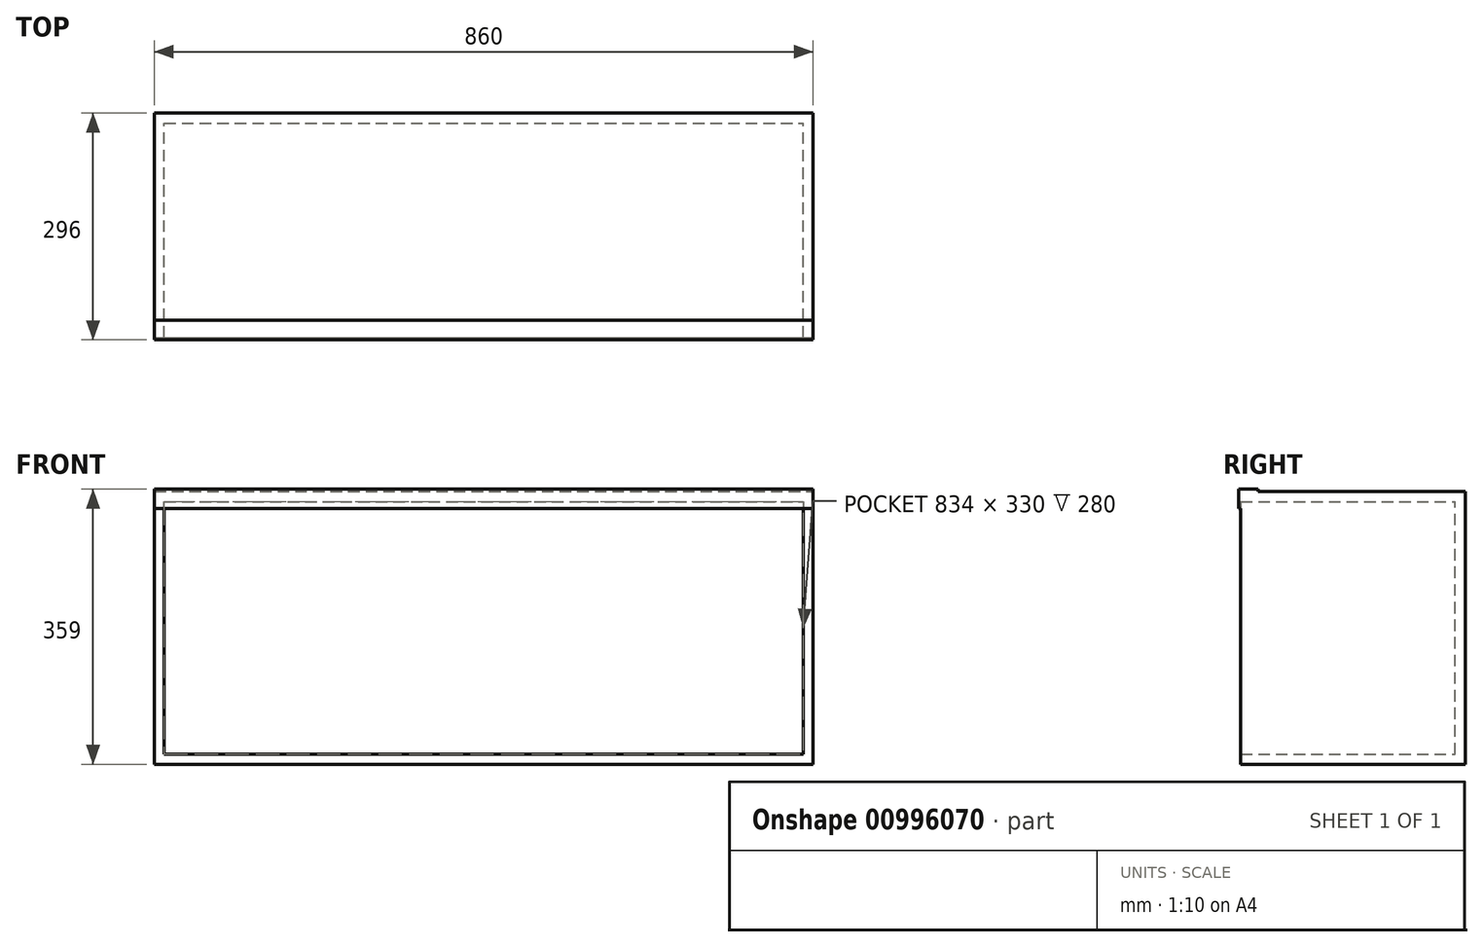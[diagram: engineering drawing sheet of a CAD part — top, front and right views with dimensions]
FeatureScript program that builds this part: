
annotation { "Feature Type Name" : "Feature", "Feature Type Description" : "" }
export const myFeature = defineFeature(function(context is Context, id is Id, definition is map)
    precondition{}
    {
        {
            var Q0;
            Q0=qCreatedBy(makeId("Front.planeOp"),FACE);
            var sketch = newSketch(context, id + "F0", { "sketchPlane" : qUnion([Q0])});
            skLineSegment(sketch, "E0.bottom", {"start": v(-430, 178) * mm, "end": v(430, 178) * mm});
            skLineSegment(sketch, "E0.top", {"start": v(-430, -178) * mm, "end": v(430, -178) * mm});
            skLineSegment(sketch, "E0.left", {"start": v(-430, 178) * mm, "end": v(-430, -178) * mm});
            skLineSegment(sketch, "E0.right", {"start": v(430, 178) * mm, "end": v(430, -178) * mm});
            skPoint(sketch, "E0.middle", {"position": v(0, 0) * mm});
            skSolve(sketch);
        }
        {
            var Q0;
            Q0 = qSketchRegion(id + "F0", true);
            extrude(context, id + "F1", {"entities" : qUnion([Q0]), "depth" : 13 * mm, "offsetDistance" : 25.4 * mm});
        }
        {
            var Q0;
            Q0=makeQuery(id+"F1.opExtrude","CAP_FACE",FACE,{"disambiguationData":[OSD([sQuery(id+"F0.wireOp",EDGE,"E0.bottom"),sQuery(id+"F0.wireOp",EDGE,"E0.top"),sQuery(id+"F0.wireOp",EDGE,"E0.left"),sQuery(id+"F0.wireOp",EDGE,"E0.right")])],"isStart":false});
            var sketch = newSketch(context, id + "F2", { "sketchPlane" : qUnion([Q0])});
            skLineSegment(sketch, "E1.bottom", {"start": v(-430, -178) * mm, "end": v(-417, -178) * mm});
            skLineSegment(sketch, "E1.top", {"start": v(-430, 178) * mm, "end": v(-417, 178) * mm});
            skLineSegment(sketch, "E1.left", {"start": v(-430, -178) * mm, "end": v(-430, 178) * mm});
            skLineSegment(sketch, "E1.right", {"start": v(-417, -178) * mm, "end": v(-417, 178) * mm});
            skLineSegment(sketch, "E2.bottom", {"start": v(430, 178) * mm, "end": v(417, 178) * mm});
            skLineSegment(sketch, "E2.top", {"start": v(430, -178) * mm, "end": v(417, -178) * mm});
            skLineSegment(sketch, "E2.left", {"start": v(430, 178) * mm, "end": v(430, -178) * mm});
            skLineSegment(sketch, "E2.right", {"start": v(417, 178) * mm, "end": v(417, -178) * mm});
            skSolve(sketch);
        }
        {
            var Q0;
            Q0 = qSketchRegion(id + "F2", true);
            extrude(context, id + "F3", {"entities" : qUnion([Q0]), "operationType" : NewBodyOperationType.ADD, "depth" : 280 * mm, "offsetDistance" : 25.4 * mm});
        }
        {
            var Q0;
            Q0=makeQuery(id+"F1.opExtrude","CAP_FACE",FACE,{"disambiguationData":[OSD([sQuery(id+"F0.wireOp",EDGE,"E0.bottom"),sQuery(id+"F0.wireOp",EDGE,"E0.top"),sQuery(id+"F0.wireOp",EDGE,"E0.left"),sQuery(id+"F0.wireOp",EDGE,"E0.right")])],"isStart":false});
            var sketch = newSketch(context, id + "F4", { "sketchPlane" : qUnion([Q0])});
            skLineSegment(sketch, "E3.bottom", {"start": v(-417, 178) * mm, "end": v(417, 178) * mm});
            skLineSegment(sketch, "E3.top", {"start": v(-417, 165) * mm, "end": v(417, 165) * mm});
            skLineSegment(sketch, "E3.left", {"start": v(-417, 178) * mm, "end": v(-417, 165) * mm});
            skLineSegment(sketch, "E3.right", {"start": v(417, 178) * mm, "end": v(417, 165) * mm});
            skLineSegment(sketch, "E4.bottom", {"start": v(-417, -178) * mm, "end": v(417, -178) * mm});
            skLineSegment(sketch, "E4.top", {"start": v(-417, -165) * mm, "end": v(417, -165) * mm});
            skLineSegment(sketch, "E4.left", {"start": v(-417, -178) * mm, "end": v(-417, -165) * mm});
            skLineSegment(sketch, "E4.right", {"start": v(417, -178) * mm, "end": v(417, -165) * mm});
            skSolve(sketch);
        }
        {
            var Q0;
            Q0 = qSketchRegion(id + "F4", true);
            extrude(context, id + "F5", {"entities" : qUnion([Q0]), "operationType" : NewBodyOperationType.ADD, "depth" : 280 * mm, "offsetDistance" : 25.4 * mm});
        }
        {
            var Q0;
            Q0=makeQuery(id+"F3.boolean.opBoolean","MERGE",FACE,{"derivedFrom":[makeQuery(id+"F1.opExtrude","SWEPT_FACE",FACE,{"disambiguationData":[OSD([sQuery(id+"F0.wireOp",EDGE,"E0.right")])]}),makeQuery(id+"F3.opExtrude","SWEPT_FACE",FACE,{"disambiguationData":[OSD([sQuery(id+"F2.wireOp",EDGE,"E2.left")])]})]});
            var sketch = newSketch(context, id + "F6", { "sketchPlane" : qUnion([Q0])});
            skLineSegment(sketch, "E5", {"start": v(-270.6, 181) * mm, "end": v(-296, 181) * mm});
            skLineSegment(sketch, "E6", {"start": v(-296, 181) * mm, "end": v(-296, 155.6) * mm});
            skLineSegment(sketch, "E7", {"start": v(-296, 155.6) * mm, "end": v(-293, 155.6) * mm});
            skLineSegment(sketch, "E8", {"start": v(-293, 155.6) * mm, "end": v(-293, 178) * mm});
            skLineSegment(sketch, "E9", {"start": v(-293, 178) * mm, "end": v(-270.6, 178) * mm});
            skLineSegment(sketch, "E10", {"start": v(-270.6, 178) * mm, "end": v(-270.6, 181) * mm});
            skSolve(sketch);
        }
        {
            var Q0;
            Q0 = qSketchRegion(id + "F6", true);
            var Q1;
            Q1=makeQuery(id+"F3.boolean.opBoolean","MERGE",FACE,{"derivedFrom":[makeQuery(id+"F1.opExtrude","SWEPT_FACE",FACE,{"disambiguationData":[OSD([sQuery(id+"F0.wireOp",EDGE,"E0.left")])]}),makeQuery(id+"F3.opExtrude","SWEPT_FACE",FACE,{"disambiguationData":[OSD([sQuery(id+"F2.wireOp",EDGE,"E1.left")])]})]});
            extrude(context, id + "F7", {"entities" : qUnion([Q0]), "operationType" : NewBodyOperationType.ADD, "endBound" : BoundingType.UP_TO_SURFACE, "oppositeDirection" : true, "depth" : 25.4 * mm, "endBoundEntityFace" : qUnion([Q1]), "offsetDistance" : 25.4 * mm});
        }
    });
